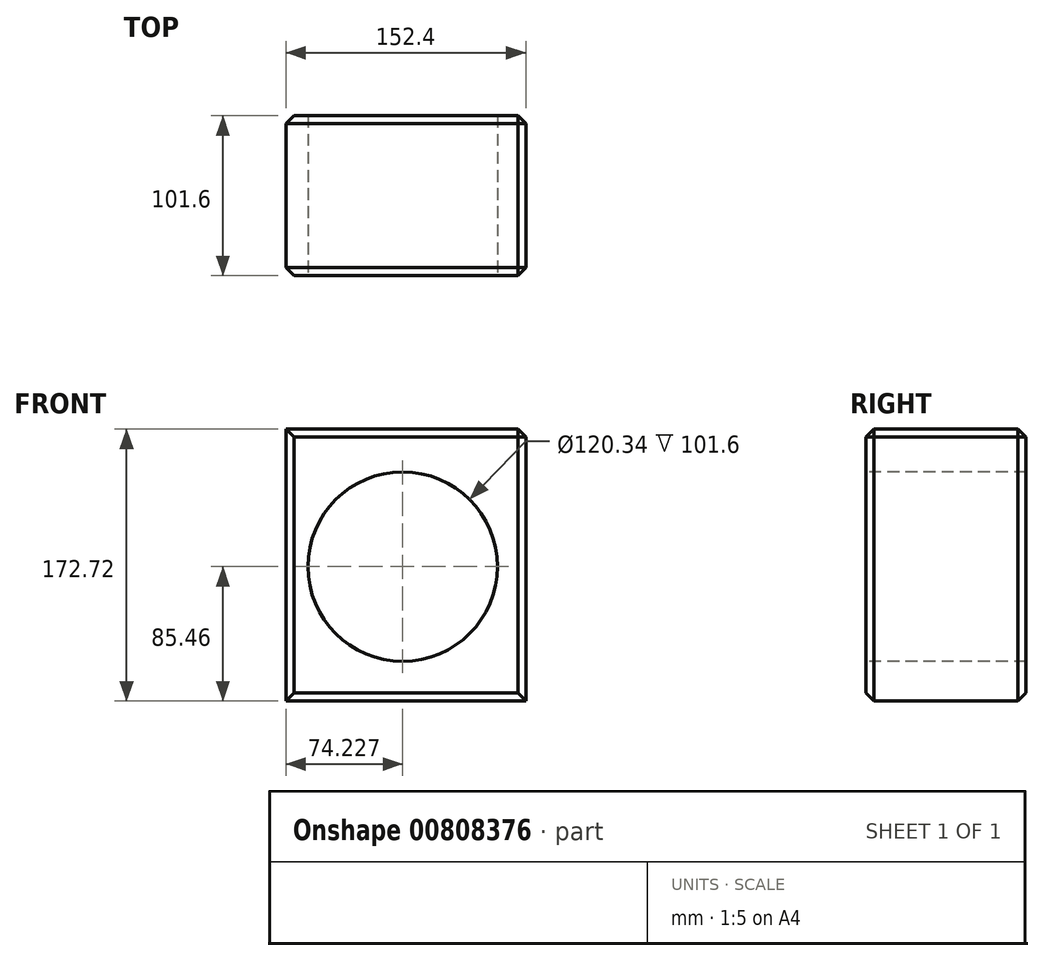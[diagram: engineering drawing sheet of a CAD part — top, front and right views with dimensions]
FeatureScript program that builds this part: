
annotation { "Feature Type Name" : "Feature", "Feature Type Description" : "" }
export const myFeature = defineFeature(function(context is Context, id is Id, definition is map)
    precondition{}
    {
        {
            var Q0;
            Q0=qCreatedBy(makeId("Front.planeOp"),FACE);
            var sketch = newSketch(context, id + "F0", { "sketchPlane" : qUnion([Q0])});
            skLineSegment(sketch, "E0.bottom", {"start": v(-65.37, 87.26) * mm, "end": v(87.03, 87.26) * mm});
            skLineSegment(sketch, "E0.top", {"start": v(-65.37, -85.46) * mm, "end": v(87.03, -85.46) * mm});
            skLineSegment(sketch, "E0.left", {"start": v(-65.37, 87.26) * mm, "end": v(-65.37, -85.46) * mm});
            skLineSegment(sketch, "E0.right", {"start": v(87.03, 87.26) * mm, "end": v(87.03, -85.46) * mm});
            skSolve(sketch);
        }
        {
            var Q0;
            Q0 = qSketchRegion(id + "F0", true);
            extrude(context, id + "F1", {"entities" : qUnion([Q0]), "depth" : 101.6 * mm, "offsetDistance" : 25.4 * mm});
        }
        {
            var Q0;
            Q0=makeQuery(id+"F1.opExtrude","CAP_FACE",FACE,{"disambiguationData":[OSD([sQuery(id+"F0.wireOp",EDGE,"E0.bottom"),sQuery(id+"F0.wireOp",EDGE,"E0.top"),sQuery(id+"F0.wireOp",EDGE,"E0.left"),sQuery(id+"F0.wireOp",EDGE,"E0.right")])],"isStart":false});
            var sketch = newSketch(context, id + "F2", { "sketchPlane" : qUnion([Q0])});
            skCircle(sketch, "E1", {"center": v(8.86, 0) * mm, "radius": 60.17 * mm});
            skSolve(sketch);
        }
        {
            var Q0;
            Q0 = qSketchRegion(id + "F2", true);
            extrude(context, id + "F3", {"entities" : qUnion([Q0]), "operationType" : NewBodyOperationType.REMOVE, "endBound" : BoundingType.THROUGH_ALL, "oppositeDirection" : true, "depth" : 25.4 * mm, "offsetDistance" : 25.4 * mm});
        }
        {
            var Q0;
            Q0=makeQuery(id+"F1.opExtrude","CAP_EDGE",EDGE,{"disambiguationData":[OSD([sQuery(id+"F0.wireOp",EDGE,"E0.right")])],"isStart":false});
            var Q1;
            Q1=makeQuery(id+"F1.opExtrude","CAP_EDGE",EDGE,{"disambiguationData":[OSD([sQuery(id+"F0.wireOp",EDGE,"E0.bottom")])],"isStart":false});
            var Q2;
            Q2=makeQuery(id+"F1.opExtrude","CAP_EDGE",EDGE,{"disambiguationData":[OSD([sQuery(id+"F0.wireOp",EDGE,"E0.top")])],"isStart":false});
            var Q3;
            Q3=makeQuery(id+"F1.opExtrude","CAP_EDGE",EDGE,{"disambiguationData":[OSD([sQuery(id+"F0.wireOp",EDGE,"E0.left")])],"isStart":false});
            var Q4;
            Q4=makeQuery(id+"F1.opExtrude","CAP_EDGE",EDGE,{"disambiguationData":[OSD([sQuery(id+"F0.wireOp",EDGE,"E0.top")])],"isStart":true});
            var Q5;
            Q5=makeQuery(id+"F1.opExtrude","CAP_EDGE",EDGE,{"disambiguationData":[OSD([sQuery(id+"F0.wireOp",EDGE,"E0.left")])],"isStart":true});
            var Q6;
            Q6=makeQuery(id+"F1.opExtrude","CAP_EDGE",EDGE,{"disambiguationData":[OSD([sQuery(id+"F0.wireOp",EDGE,"E0.right")])],"isStart":true});
            var Q7;
            Q7=makeQuery(id+"F1.opExtrude","CAP_EDGE",EDGE,{"disambiguationData":[OSD([sQuery(id+"F0.wireOp",EDGE,"E0.bottom")])],"isStart":true});
            var Q8;
            Q8=makeQuery(id+"F1.opExtrude","SWEPT_EDGE",EDGE,{"disambiguationData":[OSD([sQuery(id+"F0.wireOp",EDGE,"E0.bottom"),sQuery(id+"F0.wireOp",EDGE,"E0.right")])]});
            chamfer(context, id + "F4", {"entities" : qUnion([Q0, Q1, Q2, Q3, Q4, Q5, Q6, Q7, Q8]), "width" : 5.08 * mm, "tangentPropagation" : true});
        }
    });
